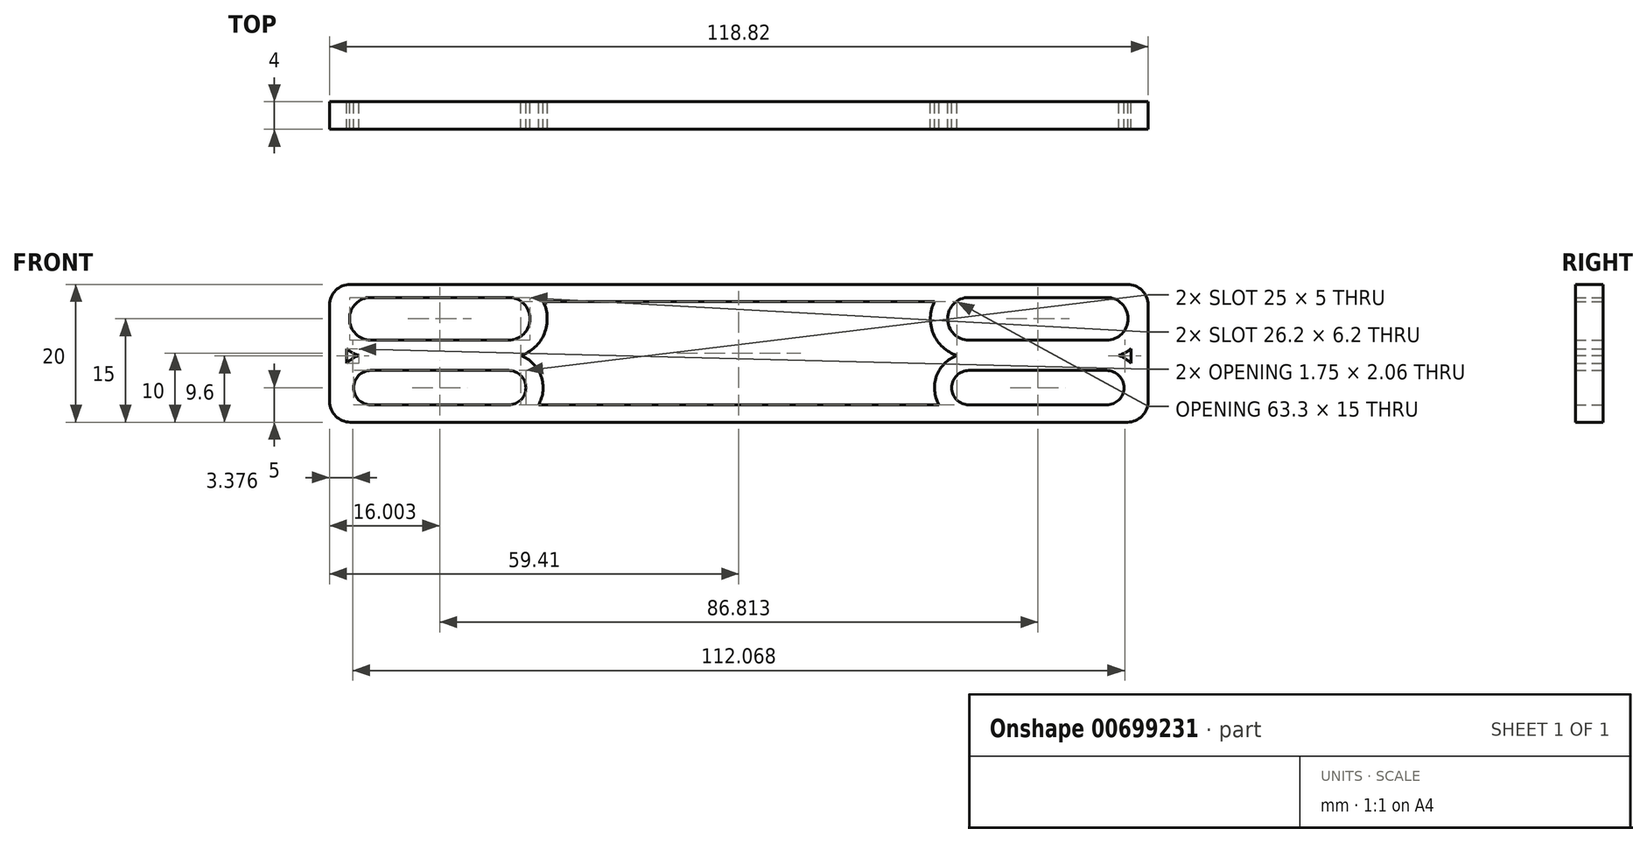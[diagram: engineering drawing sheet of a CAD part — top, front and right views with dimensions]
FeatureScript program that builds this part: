
annotation { "Feature Type Name" : "Feature", "Feature Type Description" : "" }
export const myFeature = defineFeature(function(context is Context, id is Id, definition is map)
    precondition{}
    {
        {
            var Q0;
            Q0=qCreatedBy(makeId("Front.planeOp"),FACE);
            var sketch = newSketch(context, id + "F0", { "sketchPlane" : qUnion([Q0])});
            skLineSegment(sketch, "E0.bottom", {"start": v(59.4, 10) * mm, "end": v(-59.4, 10) * mm});
            skLineSegment(sketch, "E0.top", {"start": v(59.4, -10) * mm, "end": v(-59.4, -10) * mm});
            skLineSegment(sketch, "E0.left", {"start": v(59.4, 10) * mm, "end": v(59.4, -10) * mm});
            skLineSegment(sketch, "E0.right", {"start": v(-59.4, 10) * mm, "end": v(-59.4, -10) * mm});
            skPoint(sketch, "E0.middle", {"position": v(0, 0) * mm});
            skLineSegment(sketch, "E1", {"start": v(-53.4, 5) * mm, "end": v(-33.4, 5) * mm});
            skLineSegment(sketch, "E2", {"start": v(33.4, 5) * mm, "end": v(53.4, 5) * mm});
            skArc(sketch, "E3.0.startCap", {"start": v(-53.4, 1.9) * mm, "mid": v(-56.5, 5) * mm, "end": v(-53.4, 8.1) * mm});
            skArc(sketch, "E3.0.endCap", {"start": v(-33.4, 8.1) * mm, "mid": v(-30.3, 5) * mm, "end": v(-33.4, 1.9) * mm});
            skLineSegment(sketch, "E3.0.left", {"start": v(-53.4, 8.1) * mm, "end": v(-33.4, 8.1) * mm});
            skLineSegment(sketch, "E3.0.right", {"start": v(-53.4, 1.9) * mm, "end": v(-33.4, 1.9) * mm});
            skArc(sketch, "E4.0.startCap", {"start": v(33.4, 1.9) * mm, "mid": v(30.3, 5) * mm, "end": v(33.4, 8.1) * mm});
            skArc(sketch, "E4.0.endCap", {"start": v(53.4, 8.1) * mm, "mid": v(56.5, 5) * mm, "end": v(53.4, 1.9) * mm});
            skLineSegment(sketch, "E4.0.left", {"start": v(33.4, 8.1) * mm, "end": v(53.4, 8.1) * mm});
            skLineSegment(sketch, "E4.0.right", {"start": v(33.4, 1.9) * mm, "end": v(53.4, 1.9) * mm});
            skLineSegment(sketch, "E5", {"start": v(33.4, -5) * mm, "end": v(53.4, -5) * mm});
            skLineSegment(sketch, "E6", {"start": v(-53.4, -5) * mm, "end": v(-33.4, -5) * mm});
            skArc(sketch, "E7.0.startCap", {"start": v(-53.4, -7.5) * mm, "mid": v(-55.9, -5) * mm, "end": v(-53.4, -2.5) * mm});
            skArc(sketch, "E7.0.endCap", {"start": v(-33.4, -2.5) * mm, "mid": v(-30.9, -5) * mm, "end": v(-33.4, -7.5) * mm});
            skLineSegment(sketch, "E7.0.left", {"start": v(-53.4, -2.5) * mm, "end": v(-33.4, -2.5) * mm});
            skLineSegment(sketch, "E7.0.right", {"start": v(-53.4, -7.5) * mm, "end": v(-33.4, -7.5) * mm});
            skArc(sketch, "E8.0.startCap", {"start": v(33.4, -7.5) * mm, "mid": v(30.9, -5) * mm, "end": v(33.4, -2.5) * mm});
            skArc(sketch, "E8.0.endCap", {"start": v(53.4, -2.5) * mm, "mid": v(55.9, -5) * mm, "end": v(53.4, -7.5) * mm});
            skLineSegment(sketch, "E8.0.left", {"start": v(33.4, -2.5) * mm, "end": v(53.4, -2.5) * mm});
            skLineSegment(sketch, "E8.0.right", {"start": v(33.4, -7.5) * mm, "end": v(53.4, -7.5) * mm});
            skSolve(sketch);
        }
        {
            var Q0;
            Q0=makeQuery(id+"F0.imprint","IMPRINT",FACE,{"disambiguationData":[TD([[makeQuery(id+"F0.imprint","IMPRINT",EDGE,{"derivedFrom":sQuery(id+"F0.wireOp",EDGE,"E0.bottom")}),1.0]])]});
            extrude(context, id + "F1", {"entities" : qUnion([Q0]), "depth" : 4 * mm, "offsetDistance" : 25 * mm});
        }
        {
            var Q0;
            Q0=makeQuery(id+"F1.opExtrude","CAP_FACE",FACE,{"disambiguationData":[OSD([sQuery(id+"F0.wireOp",EDGE,"E0.bottom"),sQuery(id+"F0.wireOp",EDGE,"E0.top"),sQuery(id+"F0.wireOp",EDGE,"E0.left"),sQuery(id+"F0.wireOp",EDGE,"E0.right"),sQuery(id+"F0.wireOp",EDGE,"E3.0.startCap"),sQuery(id+"F0.wireOp",EDGE,"E3.0.endCap"),sQuery(id+"F0.wireOp",EDGE,"E3.0.left"),sQuery(id+"F0.wireOp",EDGE,"E3.0.right"),sQuery(id+"F0.wireOp",EDGE,"E4.0.startCap"),sQuery(id+"F0.wireOp",EDGE,"E4.0.endCap"),sQuery(id+"F0.wireOp",EDGE,"E4.0.left"),sQuery(id+"F0.wireOp",EDGE,"E4.0.right"),sQuery(id+"F0.wireOp",EDGE,"E7.0.startCap"),sQuery(id+"F0.wireOp",EDGE,"E7.0.endCap"),sQuery(id+"F0.wireOp",EDGE,"E7.0.left"),sQuery(id+"F0.wireOp",EDGE,"E7.0.right"),sQuery(id+"F0.wireOp",EDGE,"E8.0.startCap"),sQuery(id+"F0.wireOp",EDGE,"E8.0.endCap"),sQuery(id+"F0.wireOp",EDGE,"E8.0.left"),sQuery(id+"F0.wireOp",EDGE,"E8.0.right")])],"isStart":false});
            var Q1;
            Q1=makeQuery(id+"F1.opExtrude","CAP_FACE",FACE,{"disambiguationData":[OSD([sQuery(id+"F0.wireOp",EDGE,"E0.bottom"),sQuery(id+"F0.wireOp",EDGE,"E0.top"),sQuery(id+"F0.wireOp",EDGE,"E0.left"),sQuery(id+"F0.wireOp",EDGE,"E0.right"),sQuery(id+"F0.wireOp",EDGE,"E3.0.startCap"),sQuery(id+"F0.wireOp",EDGE,"E3.0.endCap"),sQuery(id+"F0.wireOp",EDGE,"E3.0.left"),sQuery(id+"F0.wireOp",EDGE,"E3.0.right"),sQuery(id+"F0.wireOp",EDGE,"E4.0.startCap"),sQuery(id+"F0.wireOp",EDGE,"E4.0.endCap"),sQuery(id+"F0.wireOp",EDGE,"E4.0.left"),sQuery(id+"F0.wireOp",EDGE,"E4.0.right"),sQuery(id+"F0.wireOp",EDGE,"E7.0.startCap"),sQuery(id+"F0.wireOp",EDGE,"E7.0.endCap"),sQuery(id+"F0.wireOp",EDGE,"E7.0.left"),sQuery(id+"F0.wireOp",EDGE,"E7.0.right"),sQuery(id+"F0.wireOp",EDGE,"E8.0.startCap"),sQuery(id+"F0.wireOp",EDGE,"E8.0.endCap"),sQuery(id+"F0.wireOp",EDGE,"E8.0.left"),sQuery(id+"F0.wireOp",EDGE,"E8.0.right")])],"isStart":true});
            shell(context, id + "F2", {"entities" : qUnion([Q0, Q1]), "thickness" : 2.5 * mm});
        }
        {
            var Q0;
            Q0=makeQuery(id+"F1.opExtrude","SWEPT_EDGE",EDGE,{"disambiguationData":[OSD([sQuery(id+"F0.wireOp",EDGE,"E0.top"),sQuery(id+"F0.wireOp",EDGE,"E0.left")])]});
            var Q1;
            Q1=makeQuery(id+"F1.opExtrude","SWEPT_EDGE",EDGE,{"disambiguationData":[OSD([sQuery(id+"F0.wireOp",EDGE,"E0.bottom"),sQuery(id+"F0.wireOp",EDGE,"E0.left")])]});
            var Q2;
            Q2=makeQuery(id+"F1.opExtrude","SWEPT_EDGE",EDGE,{"disambiguationData":[OSD([sQuery(id+"F0.wireOp",EDGE,"E0.top"),sQuery(id+"F0.wireOp",EDGE,"E0.right")])]});
            var Q3;
            Q3=makeQuery(id+"F1.opExtrude","SWEPT_EDGE",EDGE,{"disambiguationData":[OSD([sQuery(id+"F0.wireOp",EDGE,"E0.bottom"),sQuery(id+"F0.wireOp",EDGE,"E0.right")])]});
            fillet(context, id + "F3", {"entities" : qUnion([Q0, Q1, Q2, Q3]), "radius" : 3 * mm, "tangentPropagation" : true, "allowEdgeOverflow" : false});
        }
    });
